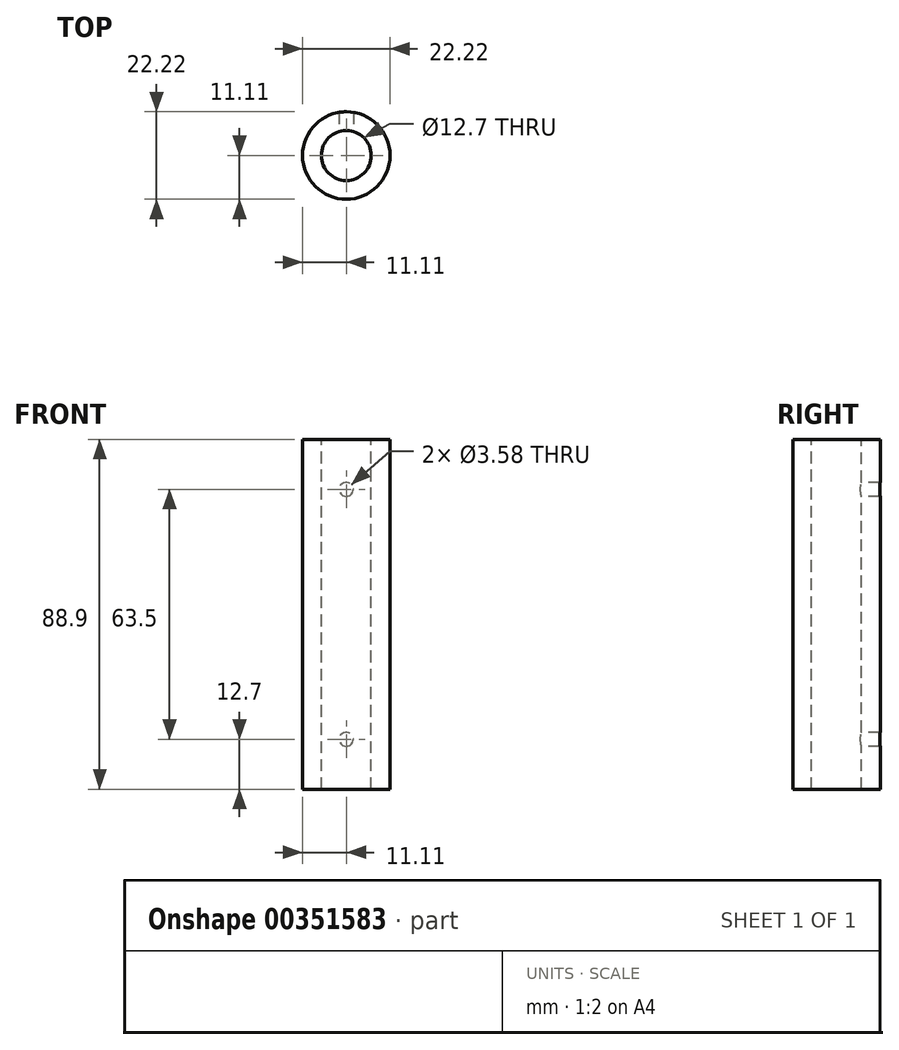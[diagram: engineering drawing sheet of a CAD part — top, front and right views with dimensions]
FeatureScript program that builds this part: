
annotation { "Feature Type Name" : "Feature", "Feature Type Description" : "" }
export const myFeature = defineFeature(function(context is Context, id is Id, definition is map)
    precondition{}
    {
        {
            var Q0;
            Q0=qCreatedBy(makeId("Top.planeOp"),FACE);
            var sketch = newSketch(context, id + "F0", { "sketchPlane" : qUnion([Q0])});
            skCircle(sketch, "E0", {"center": v(0, 0) * mm, "radius": 11.11 * mm});
            skSolve(sketch);
        }
        {
            var Q0;
            Q0 = qSketchRegion(id + "F0", true);
            extrude(context, id + "F1", {"entities" : qUnion([Q0]), "depth" : 88.9 * mm});
        }
        {
            var Q0;
            Q0=makeQuery(id+"F1.opExtrude","CAP_FACE",FACE,{"disambiguationData":[OSD([sQuery(id+"F0.wireOp",EDGE,"E0")])],"isStart":false});
            var sketch = newSketch(context, id + "F2", { "sketchPlane" : qUnion([Q0])});
            skCircle(sketch, "E1", {"center": v(0, 0) * mm, "radius": 6.35 * mm});
            skSolve(sketch);
        }
        {
            var Q0;
            Q0 = qSketchRegion(id + "F2", true);
            extrude(context, id + "F3", {"entities" : qUnion([Q0]), "operationType" : NewBodyOperationType.REMOVE, "oppositeDirection" : true, "depth" : 88.9 * mm});
        }
        {
            var Q0;
            Q0=qCreatedBy(makeId("Front.planeOp"),FACE);
            var sketch = newSketch(context, id + "F4", { "sketchPlane" : qUnion([Q0])});
            skLineSegment(sketch, "E2", {"start": v(0, 0) * mm, "end": v(0, 12.7) * mm, "construction": true});
            skLineSegment(sketch, "E3", {"start": v(0, 12.7) * mm, "end": v(0, 76.2) * mm, "construction": true});
            skCircle(sketch, "E4", {"center": v(0, 12.7) * mm, "radius": 1.8 * mm});
            skCircle(sketch, "E5", {"center": v(0, 76.2) * mm, "radius": 1.8 * mm});
            skSolve(sketch);
        }
        {
            var Q0;
            Q0 = qSketchRegion(id + "F4", true);
            extrude(context, id + "F5", {"entities" : qUnion([Q0]), "operationType" : NewBodyOperationType.REMOVE, "oppositeDirection" : true, "depth" : 22.22 * mm});
        }
    });
